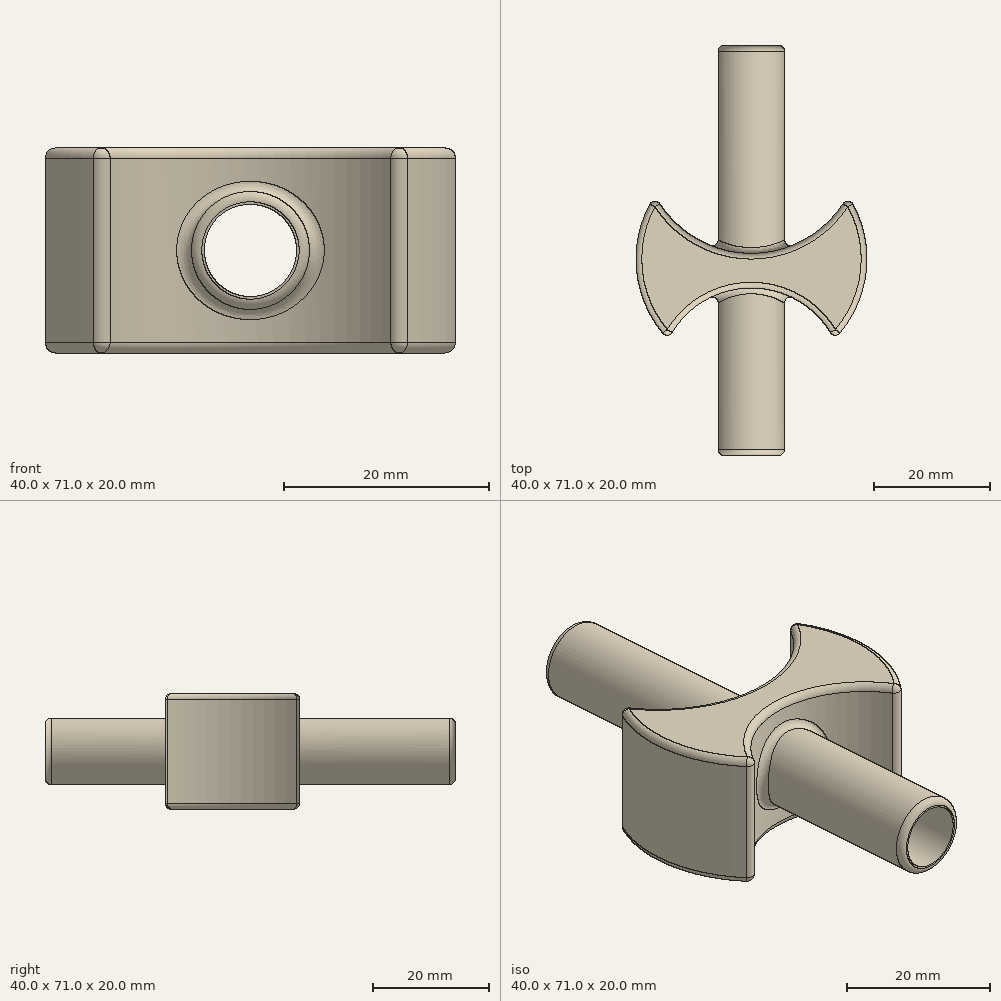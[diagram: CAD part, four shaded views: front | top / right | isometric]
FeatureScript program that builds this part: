
annotation { "Feature Type Name" : "Feature", "Feature Type Description" : "" }
export const myFeature = defineFeature(function(context is Context, id is Id, definition is map)
    precondition{}
    {
        {
            var Q0;
            Q0=qCreatedBy(makeId("Top.planeOp"),FACE);
            var sketch = newSketch(context, id + "F0", { "sketchPlane" : qUnion([Q0])});
            skCircle(sketch, "E0", {"center": v(0, 0) * mm, "radius": 20 * mm});
            skCircle(sketch, "E1", {"center": v(0, 20) * mm, "radius": 19 * mm});
            skCircle(sketch, "E2", {"center": v(0, -21) * mm, "radius": 16 * mm});
            skSolve(sketch);
        }
        {
            var Q0;
            {var subQ0=sQuery(id+"F0.wireOp",EDGE,"E1");var subQ1=sQuery(id+"F0.wireOp",EDGE,"E0");var subQ2=makeQuery(id+"F0.imprint","INTERSECT",VERTEX,{"disambiguationData":[OD(0.0)],"derivedFrom":[subQ1,subQ0]});Q0=makeQuery(id+"F0.imprint","IMPRINT",FACE,{"disambiguationData":[TD([[makeQuery(id+"F0.imprint","IMPRINT",EDGE,{"disambiguationData":[TD([[subQ2,-1.0]])],"derivedFrom":subQ1}),1.0]])]});}
            extrude(context, id + "F1", {"entities" : qUnion([Q0]), "endBound" : BoundingType.SYMMETRIC, "depth" : 20 * mm});
        }
        {
            var Q0;
            Q0=qCreatedBy(makeId("Front.planeOp"),FACE);
            var sketch = newSketch(context, id + "F2", { "sketchPlane" : qUnion([Q0])});
            skCircle(sketch, "E3", {"center": v(0, 0) * mm, "radius": 5.75 * mm});
            skSolve(sketch);
        }
        {
            var Q0;
            Q0 = qSketchRegion(id + "F2", true);
            extrude(context, id + "F3", {"entities" : qUnion([Q0]), "operationType" : NewBodyOperationType.ADD, "depth" : 34 * mm, "hasSecondDirection" : true, "secondDirectionOppositeDirection" : true, "secondDirectionDepth" : (71 - 34) * mm});
        }
        {
            var Q0;
            Q0=makeQuery(id+"F3.opExtrude","CAP_FACE",FACE,{"disambiguationData":[OSD([sQuery(id+"F2.wireOp",EDGE,"E3")])],"isStart":false});
            var sketch = newSketch(context, id + "F4", { "sketchPlane" : qUnion([Q0])});
            skCircle(sketch, "E4", {"center": v(0, 0) * mm, "radius": 4.5 * mm});
            skSolve(sketch);
        }
        {
            var Q0;
            Q0 = qSketchRegion(id + "F4", true);
            extrude(context, id + "F5", {"entities" : qUnion([Q0]), "operationType" : NewBodyOperationType.REMOVE, "endBound" : BoundingType.THROUGH_ALL, "oppositeDirection" : true, "depth" : 25 * mm});
        }
        {
            var Q0;
            Q0=makeQuery(id+"F1.opExtrude","CAP_FACE",FACE,{"disambiguationData":[OSD([sQuery(id+"F0.wireOp",EDGE,"E0"),sQuery(id+"F0.wireOp",EDGE,"E1"),sQuery(id+"F0.wireOp",EDGE,"E2")])],"isStart":true});
            var Q1;
            Q1=makeQuery(id+"F1.opExtrude","CAP_FACE",FACE,{"disambiguationData":[OSD([sQuery(id+"F0.wireOp",EDGE,"E0"),sQuery(id+"F0.wireOp",EDGE,"E1"),sQuery(id+"F0.wireOp",EDGE,"E2")])],"isStart":false});
            var Q2;
            {var subQ0=sQuery(id+"F0.wireOp",EDGE,"E2");var subQ1=sQuery(id+"F0.wireOp",EDGE,"E0");Q2=makeQuery(id+"F1.opExtrude","SWEPT_EDGE",EDGE,{"disambiguationData":[OSD([subQ1,subQ0]),TDD([makeQuery(id+"F0.imprint","INTERSECT",VERTEX,{"disambiguationData":[OD(0.0)],"derivedFrom":[subQ1,subQ0]})])]});}
            var Q3;
            {var subQ0=sQuery(id+"F0.wireOp",EDGE,"E2");var subQ1=sQuery(id+"F0.wireOp",EDGE,"E0");Q3=makeQuery(id+"F1.opExtrude","SWEPT_EDGE",EDGE,{"disambiguationData":[OSD([subQ1,subQ0]),TDD([makeQuery(id+"F0.imprint","INTERSECT",VERTEX,{"disambiguationData":[OD(1.0)],"derivedFrom":[subQ1,subQ0]})])]});}
            var Q4;
            {var subQ0=sQuery(id+"F0.wireOp",EDGE,"E1");var subQ1=sQuery(id+"F0.wireOp",EDGE,"E0");Q4=makeQuery(id+"F1.opExtrude","SWEPT_EDGE",EDGE,{"disambiguationData":[OSD([subQ1,subQ0]),TDD([makeQuery(id+"F0.imprint","INTERSECT",VERTEX,{"disambiguationData":[OD(0.0)],"derivedFrom":[subQ1,subQ0]})])]});}
            var Q5;
            {var subQ0=sQuery(id+"F0.wireOp",EDGE,"E1");var subQ1=sQuery(id+"F0.wireOp",EDGE,"E0");Q5=makeQuery(id+"F1.opExtrude","SWEPT_EDGE",EDGE,{"disambiguationData":[OSD([subQ1,subQ0]),TDD([makeQuery(id+"F0.imprint","INTERSECT",VERTEX,{"disambiguationData":[OD(1.0)],"derivedFrom":[subQ1,subQ0]})])]});}
            var Q6;
            Q6=makeQuery(id+"F3.opExtrude","CAP_EDGE",EDGE,{"disambiguationData":[OSD([sQuery(id+"F2.wireOp",EDGE,"E3")])],"isStart":false});
            var Q7;
            Q7=makeQuery(id+"F3.opExtrude","CAP_EDGE",EDGE,{"disambiguationData":[OSD([sQuery(id+"F2.wireOp",EDGE,"E3")])],"isStart":true});
            var Q8;
            Q8=makeQuery(id+"F3.boolean.opBoolean","INTERSECT",EDGE,{"derivedFrom":[makeQuery(id+"F1.opExtrude","SWEPT_FACE",FACE,{"disambiguationData":[OSD([sQuery(id+"F0.wireOp",EDGE,"E2")])]}),makeQuery(id+"F3.opExtrude","SWEPT_FACE",FACE,{"disambiguationData":[OSD([sQuery(id+"F2.wireOp",EDGE,"E3")])]})]});
            var Q9;
            Q9=makeQuery(id+"F3.boolean.opBoolean","INTERSECT",EDGE,{"derivedFrom":[makeQuery(id+"F1.opExtrude","SWEPT_FACE",FACE,{"disambiguationData":[OSD([sQuery(id+"F0.wireOp",EDGE,"E1")])]}),makeQuery(id+"F3.opExtrude","SWEPT_FACE",FACE,{"disambiguationData":[OSD([sQuery(id+"F2.wireOp",EDGE,"E3")])]})]});
            fillet(context, id + "F6", {"entities" : qUnion([Q0, Q1, Q2, Q3, Q4, Q5, Q6, Q7, Q8, Q9]), "radius" : 1 * mm, "tangentPropagation" : true, "allowEdgeOverflow" : false});
        }
    });
